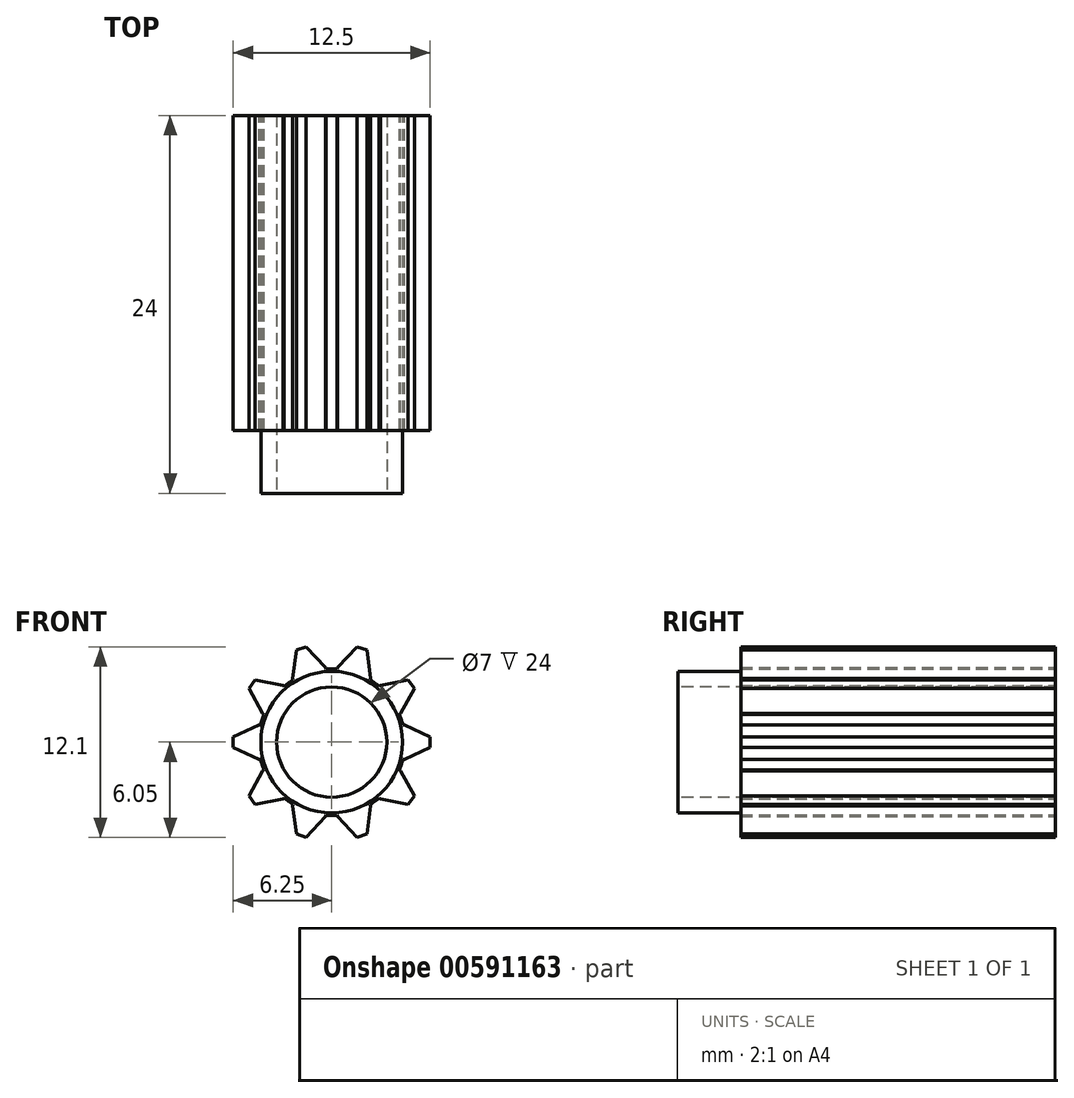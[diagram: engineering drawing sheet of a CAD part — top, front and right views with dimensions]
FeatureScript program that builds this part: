
annotation { "Feature Type Name" : "Feature", "Feature Type Description" : "" }
export const myFeature = defineFeature(function(context is Context, id is Id, definition is map)
    precondition{}
    {
        {
            var Q0;
            Q0=qCreatedBy(makeId("Front.planeOp"),FACE);
            var sketch = newSketch(context, id + "F0", { "sketchPlane" : qUnion([Q0])});
            skCircle(sketch, "E0", {"center": v(0, 0) * mm, "radius": 4.65 * mm});
            skLineSegment(sketch, "E1", {"start": v(0, 0) * mm, "end": v(4.65, 0) * mm, "construction": true});
            skLineSegment(sketch, "E2", {"start": v(4.65, 0) * mm, "end": v(6.25, 0) * mm, "construction": true});
            skLineSegment(sketch, "E3", {"start": v(6.25, 0) * mm, "end": v(6.25, 0.33) * mm});
            skLineSegment(sketch, "E4", {"start": v(4.52, 1.1) * mm, "end": v(4.62, 1.1) * mm});
            skLineSegment(sketch, "E5", {"start": v(4.62, 1.1) * mm, "end": v(6.25, 0.33) * mm});
            skLineSegment(sketch, "E6.MirrorCS", {"start": v(4.62, -1.1) * mm, "end": v(6.25, -0.33) * mm});
            skLineSegment(sketch, "E7.MirrorCS", {"start": v(6.25, 0) * mm, "end": v(6.25, -0.33) * mm});
            skLineSegment(sketch, "E8.MirrorCS", {"start": v(4.52, -1.1) * mm, "end": v(4.62, -1.1) * mm});
            skLineSegment(sketch, "E9.1.0", {"start": v(3, 3.55) * mm, "end": v(3.09, 3.6) * mm});
            skLineSegment(sketch, "E9.1.1", {"start": v(4.3, 1.77) * mm, "end": v(4.38, 1.82) * mm});
            skLineSegment(sketch, "E9.1.2", {"start": v(4.38, 1.82) * mm, "end": v(5.25, 3.4) * mm});
            skLineSegment(sketch, "E9.1.3", {"start": v(3.09, 3.6) * mm, "end": v(4.86, 3.94) * mm});
            skLineSegment(sketch, "E9.1.4", {"start": v(5.06, 3.67) * mm, "end": v(4.86, 3.94) * mm});
            skLineSegment(sketch, "E9.1.5", {"start": v(5.06, 3.67) * mm, "end": v(5.25, 3.4) * mm});
            skLineSegment(sketch, "E9.2.0", {"start": v(0.35, 4.64) * mm, "end": v(0.38, 4.73) * mm});
            skLineSegment(sketch, "E9.2.1", {"start": v(2.44, 3.96) * mm, "end": v(2.47, 4.05) * mm});
            skLineSegment(sketch, "E9.2.2", {"start": v(2.47, 4.05) * mm, "end": v(2.25, 5.84) * mm});
            skLineSegment(sketch, "E9.2.3", {"start": v(0.38, 4.73) * mm, "end": v(1.62, 6.05) * mm});
            skLineSegment(sketch, "E9.2.4", {"start": v(1.93, 5.94) * mm, "end": v(1.62, 6.05) * mm});
            skLineSegment(sketch, "E9.2.5", {"start": v(1.93, 5.94) * mm, "end": v(2.25, 5.84) * mm});
            skLineSegment(sketch, "E9.3.0", {"start": v(-2.44, 3.96) * mm, "end": v(-2.47, 4.05) * mm});
            skLineSegment(sketch, "E9.3.1", {"start": v(-0.35, 4.64) * mm, "end": v(-0.38, 4.73) * mm});
            skLineSegment(sketch, "E9.3.2", {"start": v(-0.38, 4.73) * mm, "end": v(-1.62, 6.05) * mm});
            skLineSegment(sketch, "E9.3.3", {"start": v(-2.47, 4.05) * mm, "end": v(-2.25, 5.84) * mm});
            skLineSegment(sketch, "E9.3.4", {"start": v(-1.93, 5.94) * mm, "end": v(-2.25, 5.84) * mm});
            skLineSegment(sketch, "E9.3.5", {"start": v(-1.93, 5.94) * mm, "end": v(-1.62, 6.05) * mm});
            skLineSegment(sketch, "E9.4.0", {"start": v(-4.3, 1.77) * mm, "end": v(-4.38, 1.82) * mm});
            skLineSegment(sketch, "E9.4.1", {"start": v(-3, 3.55) * mm, "end": v(-3.09, 3.6) * mm});
            skLineSegment(sketch, "E9.4.2", {"start": v(-3.09, 3.6) * mm, "end": v(-4.86, 3.94) * mm});
            skLineSegment(sketch, "E9.4.3", {"start": v(-4.38, 1.82) * mm, "end": v(-5.25, 3.4) * mm});
            skLineSegment(sketch, "E9.4.4", {"start": v(-5.06, 3.67) * mm, "end": v(-5.25, 3.4) * mm});
            skLineSegment(sketch, "E9.4.5", {"start": v(-5.06, 3.67) * mm, "end": v(-4.86, 3.94) * mm});
            skLineSegment(sketch, "E9.5.0", {"start": v(-4.52, -1.1) * mm, "end": v(-4.62, -1.1) * mm});
            skLineSegment(sketch, "E9.5.1", {"start": v(-4.52, 1.1) * mm, "end": v(-4.62, 1.1) * mm});
            skLineSegment(sketch, "E9.5.2", {"start": v(-4.62, 1.1) * mm, "end": v(-6.25, 0.33) * mm});
            skLineSegment(sketch, "E9.5.3", {"start": v(-4.62, -1.1) * mm, "end": v(-6.25, -0.33) * mm});
            skLineSegment(sketch, "E9.5.4", {"start": v(-6.25, 0) * mm, "end": v(-6.25, -0.33) * mm});
            skLineSegment(sketch, "E9.5.5", {"start": v(-6.25, 0) * mm, "end": v(-6.25, 0.33) * mm});
            skLineSegment(sketch, "E9.6.0", {"start": v(-3, -3.55) * mm, "end": v(-3.09, -3.6) * mm});
            skLineSegment(sketch, "E9.6.1", {"start": v(-4.3, -1.77) * mm, "end": v(-4.38, -1.82) * mm});
            skLineSegment(sketch, "E9.6.2", {"start": v(-4.38, -1.82) * mm, "end": v(-5.25, -3.4) * mm});
            skLineSegment(sketch, "E9.6.3", {"start": v(-3.09, -3.6) * mm, "end": v(-4.86, -3.94) * mm});
            skLineSegment(sketch, "E9.6.4", {"start": v(-5.06, -3.67) * mm, "end": v(-4.86, -3.94) * mm});
            skLineSegment(sketch, "E9.6.5", {"start": v(-5.06, -3.67) * mm, "end": v(-5.25, -3.4) * mm});
            skLineSegment(sketch, "E9.7.0", {"start": v(-0.35, -4.64) * mm, "end": v(-0.38, -4.73) * mm});
            skLineSegment(sketch, "E9.7.1", {"start": v(-2.44, -3.96) * mm, "end": v(-2.47, -4.05) * mm});
            skLineSegment(sketch, "E9.7.2", {"start": v(-2.47, -4.05) * mm, "end": v(-2.25, -5.84) * mm});
            skLineSegment(sketch, "E9.7.3", {"start": v(-0.38, -4.73) * mm, "end": v(-1.62, -6.05) * mm});
            skLineSegment(sketch, "E9.7.4", {"start": v(-1.93, -5.94) * mm, "end": v(-1.62, -6.05) * mm});
            skLineSegment(sketch, "E9.7.5", {"start": v(-1.93, -5.94) * mm, "end": v(-2.25, -5.84) * mm});
            skLineSegment(sketch, "E9.8.0", {"start": v(2.44, -3.96) * mm, "end": v(2.47, -4.05) * mm});
            skLineSegment(sketch, "E9.8.1", {"start": v(0.35, -4.64) * mm, "end": v(0.38, -4.73) * mm});
            skLineSegment(sketch, "E9.8.2", {"start": v(0.38, -4.73) * mm, "end": v(1.62, -6.05) * mm});
            skLineSegment(sketch, "E9.8.3", {"start": v(2.47, -4.05) * mm, "end": v(2.25, -5.84) * mm});
            skLineSegment(sketch, "E9.8.4", {"start": v(1.93, -5.94) * mm, "end": v(2.25, -5.84) * mm});
            skLineSegment(sketch, "E9.8.5", {"start": v(1.93, -5.94) * mm, "end": v(1.62, -6.05) * mm});
            skLineSegment(sketch, "E9.9.0", {"start": v(4.3, -1.77) * mm, "end": v(4.38, -1.82) * mm});
            skLineSegment(sketch, "E9.9.1", {"start": v(3, -3.55) * mm, "end": v(3.09, -3.6) * mm});
            skLineSegment(sketch, "E9.9.2", {"start": v(3.09, -3.6) * mm, "end": v(4.86, -3.94) * mm});
            skLineSegment(sketch, "E9.9.3", {"start": v(4.38, -1.82) * mm, "end": v(5.25, -3.4) * mm});
            skLineSegment(sketch, "E9.9.4", {"start": v(5.06, -3.67) * mm, "end": v(5.25, -3.4) * mm});
            skLineSegment(sketch, "E9.9.5", {"start": v(5.06, -3.67) * mm, "end": v(4.86, -3.94) * mm});
            skSolve(sketch);
        }
        {
            var Q0;
            Q0=qSketchRegion(id+"F0",true);
            extrude(context, id + "F1", {"entities" : qUnion([Q0]), "depth" : 10 * mm, "offsetDistance" : 25.4 * mm, "hasSecondDirection" : true, "secondDirectionOppositeDirection" : true, "secondDirectionDepth" : 10 * mm});
        }
        {
            var Q0;
            Q0=makeQuery(id+"F1.opExtrude","CAP_FACE",FACE,{"disambiguationData":[OSD([sQuery(id+"F0.wireOp",EDGE,"E0"),sQuery(id+"F0.wireOp",EDGE,"E3"),sQuery(id+"F0.wireOp",EDGE,"E4"),sQuery(id+"F0.wireOp",EDGE,"E5"),sQuery(id+"F0.wireOp",EDGE,"E6.MirrorCS"),sQuery(id+"F0.wireOp",EDGE,"E7.MirrorCS"),sQuery(id+"F0.wireOp",EDGE,"E8.MirrorCS"),sQuery(id+"F0.wireOp",EDGE,"9f6130ec-3d1a-4bbb-9d9a-4e7b52390a97.1.0"),sQuery(id+"F0.wireOp",EDGE,"9f6130ec-3d1a-4bbb-9d9a-4e7b52390a97.1.1"),sQuery(id+"F0.wireOp",EDGE,"9f6130ec-3d1a-4bbb-9d9a-4e7b52390a97.1.2"),sQuery(id+"F0.wireOp",EDGE,"9f6130ec-3d1a-4bbb-9d9a-4e7b52390a97.1.3"),sQuery(id+"F0.wireOp",EDGE,"9f6130ec-3d1a-4bbb-9d9a-4e7b52390a97.1.4"),sQuery(id+"F0.wireOp",EDGE,"9f6130ec-3d1a-4bbb-9d9a-4e7b52390a97.1.5"),sQuery(id+"F0.wireOp",EDGE,"9f6130ec-3d1a-4bbb-9d9a-4e7b52390a97.2.0"),sQuery(id+"F0.wireOp",EDGE,"9f6130ec-3d1a-4bbb-9d9a-4e7b52390a97.2.1"),sQuery(id+"F0.wireOp",EDGE,"9f6130ec-3d1a-4bbb-9d9a-4e7b52390a97.2.2"),sQuery(id+"F0.wireOp",EDGE,"9f6130ec-3d1a-4bbb-9d9a-4e7b52390a97.2.3"),sQuery(id+"F0.wireOp",EDGE,"9f6130ec-3d1a-4bbb-9d9a-4e7b52390a97.2.4"),sQuery(id+"F0.wireOp",EDGE,"9f6130ec-3d1a-4bbb-9d9a-4e7b52390a97.2.5"),sQuery(id+"F0.wireOp",EDGE,"9f6130ec-3d1a-4bbb-9d9a-4e7b52390a97.3.0"),sQuery(id+"F0.wireOp",EDGE,"9f6130ec-3d1a-4bbb-9d9a-4e7b52390a97.3.1"),sQuery(id+"F0.wireOp",EDGE,"9f6130ec-3d1a-4bbb-9d9a-4e7b52390a97.3.2"),sQuery(id+"F0.wireOp",EDGE,"9f6130ec-3d1a-4bbb-9d9a-4e7b52390a97.3.3"),sQuery(id+"F0.wireOp",EDGE,"9f6130ec-3d1a-4bbb-9d9a-4e7b52390a97.3.4"),sQuery(id+"F0.wireOp",EDGE,"9f6130ec-3d1a-4bbb-9d9a-4e7b52390a97.3.5"),sQuery(id+"F0.wireOp",EDGE,"9f6130ec-3d1a-4bbb-9d9a-4e7b52390a97.4.0"),sQuery(id+"F0.wireOp",EDGE,"9f6130ec-3d1a-4bbb-9d9a-4e7b52390a97.4.1"),sQuery(id+"F0.wireOp",EDGE,"9f6130ec-3d1a-4bbb-9d9a-4e7b52390a97.4.2"),sQuery(id+"F0.wireOp",EDGE,"9f6130ec-3d1a-4bbb-9d9a-4e7b52390a97.4.3"),sQuery(id+"F0.wireOp",EDGE,"9f6130ec-3d1a-4bbb-9d9a-4e7b52390a97.4.4"),sQuery(id+"F0.wireOp",EDGE,"9f6130ec-3d1a-4bbb-9d9a-4e7b52390a97.4.5"),sQuery(id+"F0.wireOp",EDGE,"9f6130ec-3d1a-4bbb-9d9a-4e7b52390a97.5.0"),sQuery(id+"F0.wireOp",EDGE,"9f6130ec-3d1a-4bbb-9d9a-4e7b52390a97.5.1"),sQuery(id+"F0.wireOp",EDGE,"9f6130ec-3d1a-4bbb-9d9a-4e7b52390a97.5.2"),sQuery(id+"F0.wireOp",EDGE,"9f6130ec-3d1a-4bbb-9d9a-4e7b52390a97.5.3"),sQuery(id+"F0.wireOp",EDGE,"9f6130ec-3d1a-4bbb-9d9a-4e7b52390a97.5.4"),sQuery(id+"F0.wireOp",EDGE,"9f6130ec-3d1a-4bbb-9d9a-4e7b52390a97.5.5"),sQuery(id+"F0.wireOp",EDGE,"9f6130ec-3d1a-4bbb-9d9a-4e7b52390a97.6.0"),sQuery(id+"F0.wireOp",EDGE,"9f6130ec-3d1a-4bbb-9d9a-4e7b52390a97.6.1"),sQuery(id+"F0.wireOp",EDGE,"9f6130ec-3d1a-4bbb-9d9a-4e7b52390a97.6.2"),sQuery(id+"F0.wireOp",EDGE,"9f6130ec-3d1a-4bbb-9d9a-4e7b52390a97.6.3"),sQuery(id+"F0.wireOp",EDGE,"9f6130ec-3d1a-4bbb-9d9a-4e7b52390a97.6.4"),sQuery(id+"F0.wireOp",EDGE,"9f6130ec-3d1a-4bbb-9d9a-4e7b52390a97.6.5"),sQuery(id+"F0.wireOp",EDGE,"9f6130ec-3d1a-4bbb-9d9a-4e7b52390a97.7.0"),sQuery(id+"F0.wireOp",EDGE,"9f6130ec-3d1a-4bbb-9d9a-4e7b52390a97.7.1"),sQuery(id+"F0.wireOp",EDGE,"9f6130ec-3d1a-4bbb-9d9a-4e7b52390a97.7.2"),sQuery(id+"F0.wireOp",EDGE,"9f6130ec-3d1a-4bbb-9d9a-4e7b52390a97.7.3"),sQuery(id+"F0.wireOp",EDGE,"9f6130ec-3d1a-4bbb-9d9a-4e7b52390a97.7.4"),sQuery(id+"F0.wireOp",EDGE,"9f6130ec-3d1a-4bbb-9d9a-4e7b52390a97.7.5"),sQuery(id+"F0.wireOp",EDGE,"9f6130ec-3d1a-4bbb-9d9a-4e7b52390a97.8.0"),sQuery(id+"F0.wireOp",EDGE,"9f6130ec-3d1a-4bbb-9d9a-4e7b52390a97.8.1"),sQuery(id+"F0.wireOp",EDGE,"9f6130ec-3d1a-4bbb-9d9a-4e7b52390a97.8.2"),sQuery(id+"F0.wireOp",EDGE,"9f6130ec-3d1a-4bbb-9d9a-4e7b52390a97.8.3"),sQuery(id+"F0.wireOp",EDGE,"9f6130ec-3d1a-4bbb-9d9a-4e7b52390a97.8.4"),sQuery(id+"F0.wireOp",EDGE,"9f6130ec-3d1a-4bbb-9d9a-4e7b52390a97.8.5"),sQuery(id+"F0.wireOp",EDGE,"9f6130ec-3d1a-4bbb-9d9a-4e7b52390a97.9.0"),sQuery(id+"F0.wireOp",EDGE,"9f6130ec-3d1a-4bbb-9d9a-4e7b52390a97.9.1"),sQuery(id+"F0.wireOp",EDGE,"9f6130ec-3d1a-4bbb-9d9a-4e7b52390a97.9.2"),sQuery(id+"F0.wireOp",EDGE,"9f6130ec-3d1a-4bbb-9d9a-4e7b52390a97.9.3"),sQuery(id+"F0.wireOp",EDGE,"9f6130ec-3d1a-4bbb-9d9a-4e7b52390a97.9.4"),sQuery(id+"F0.wireOp",EDGE,"9f6130ec-3d1a-4bbb-9d9a-4e7b52390a97.9.5"),sQuery(id+"F0.wireOp",EDGE,"9f6130ec-3d1a-4bbb-9d9a-4e7b52390a97.10.0"),sQuery(id+"F0.wireOp",EDGE,"9f6130ec-3d1a-4bbb-9d9a-4e7b52390a97.10.1"),sQuery(id+"F0.wireOp",EDGE,"9f6130ec-3d1a-4bbb-9d9a-4e7b52390a97.10.2"),sQuery(id+"F0.wireOp",EDGE,"9f6130ec-3d1a-4bbb-9d9a-4e7b52390a97.10.3"),sQuery(id+"F0.wireOp",EDGE,"9f6130ec-3d1a-4bbb-9d9a-4e7b52390a97.10.4"),sQuery(id+"F0.wireOp",EDGE,"9f6130ec-3d1a-4bbb-9d9a-4e7b52390a97.10.5"),sQuery(id+"F0.wireOp",EDGE,"9f6130ec-3d1a-4bbb-9d9a-4e7b52390a97.11.0"),sQuery(id+"F0.wireOp",EDGE,"9f6130ec-3d1a-4bbb-9d9a-4e7b52390a97.11.1"),sQuery(id+"F0.wireOp",EDGE,"9f6130ec-3d1a-4bbb-9d9a-4e7b52390a97.11.2"),sQuery(id+"F0.wireOp",EDGE,"9f6130ec-3d1a-4bbb-9d9a-4e7b52390a97.11.3"),sQuery(id+"F0.wireOp",EDGE,"9f6130ec-3d1a-4bbb-9d9a-4e7b52390a97.11.4"),sQuery(id+"F0.wireOp",EDGE,"9f6130ec-3d1a-4bbb-9d9a-4e7b52390a97.11.5"),sQuery(id+"F0.wireOp",EDGE,"9f6130ec-3d1a-4bbb-9d9a-4e7b52390a97.12.0"),sQuery(id+"F0.wireOp",EDGE,"9f6130ec-3d1a-4bbb-9d9a-4e7b52390a97.12.1"),sQuery(id+"F0.wireOp",EDGE,"9f6130ec-3d1a-4bbb-9d9a-4e7b52390a97.12.2"),sQuery(id+"F0.wireOp",EDGE,"9f6130ec-3d1a-4bbb-9d9a-4e7b52390a97.12.3"),sQuery(id+"F0.wireOp",EDGE,"9f6130ec-3d1a-4bbb-9d9a-4e7b52390a97.12.4"),sQuery(id+"F0.wireOp",EDGE,"9f6130ec-3d1a-4bbb-9d9a-4e7b52390a97.12.5"),sQuery(id+"F0.wireOp",EDGE,"9f6130ec-3d1a-4bbb-9d9a-4e7b52390a97.13.0"),sQuery(id+"F0.wireOp",EDGE,"9f6130ec-3d1a-4bbb-9d9a-4e7b52390a97.13.1"),sQuery(id+"F0.wireOp",EDGE,"9f6130ec-3d1a-4bbb-9d9a-4e7b52390a97.13.2"),sQuery(id+"F0.wireOp",EDGE,"9f6130ec-3d1a-4bbb-9d9a-4e7b52390a97.13.3"),sQuery(id+"F0.wireOp",EDGE,"9f6130ec-3d1a-4bbb-9d9a-4e7b52390a97.13.4"),sQuery(id+"F0.wireOp",EDGE,"9f6130ec-3d1a-4bbb-9d9a-4e7b52390a97.13.5"),sQuery(id+"F0.wireOp",EDGE,"9f6130ec-3d1a-4bbb-9d9a-4e7b52390a97.14.0"),sQuery(id+"F0.wireOp",EDGE,"9f6130ec-3d1a-4bbb-9d9a-4e7b52390a97.14.1"),sQuery(id+"F0.wireOp",EDGE,"9f6130ec-3d1a-4bbb-9d9a-4e7b52390a97.14.2"),sQuery(id+"F0.wireOp",EDGE,"9f6130ec-3d1a-4bbb-9d9a-4e7b52390a97.14.3"),sQuery(id+"F0.wireOp",EDGE,"9f6130ec-3d1a-4bbb-9d9a-4e7b52390a97.14.4"),sQuery(id+"F0.wireOp",EDGE,"9f6130ec-3d1a-4bbb-9d9a-4e7b52390a97.14.5"),sQuery(id+"F0.wireOp",EDGE,"9f6130ec-3d1a-4bbb-9d9a-4e7b52390a97.15.0"),sQuery(id+"F0.wireOp",EDGE,"9f6130ec-3d1a-4bbb-9d9a-4e7b52390a97.15.1"),sQuery(id+"F0.wireOp",EDGE,"9f6130ec-3d1a-4bbb-9d9a-4e7b52390a97.15.2"),sQuery(id+"F0.wireOp",EDGE,"9f6130ec-3d1a-4bbb-9d9a-4e7b52390a97.15.3"),sQuery(id+"F0.wireOp",EDGE,"9f6130ec-3d1a-4bbb-9d9a-4e7b52390a97.15.4"),sQuery(id+"F0.wireOp",EDGE,"9f6130ec-3d1a-4bbb-9d9a-4e7b52390a97.15.5"),sQuery(id+"F0.wireOp",EDGE,"9f6130ec-3d1a-4bbb-9d9a-4e7b52390a97.16.0"),sQuery(id+"F0.wireOp",EDGE,"9f6130ec-3d1a-4bbb-9d9a-4e7b52390a97.16.1"),sQuery(id+"F0.wireOp",EDGE,"9f6130ec-3d1a-4bbb-9d9a-4e7b52390a97.16.2"),sQuery(id+"F0.wireOp",EDGE,"9f6130ec-3d1a-4bbb-9d9a-4e7b52390a97.16.3"),sQuery(id+"F0.wireOp",EDGE,"9f6130ec-3d1a-4bbb-9d9a-4e7b52390a97.16.4"),sQuery(id+"F0.wireOp",EDGE,"9f6130ec-3d1a-4bbb-9d9a-4e7b52390a97.16.5"),sQuery(id+"F0.wireOp",EDGE,"9f6130ec-3d1a-4bbb-9d9a-4e7b52390a97.17.0"),sQuery(id+"F0.wireOp",EDGE,"9f6130ec-3d1a-4bbb-9d9a-4e7b52390a97.17.1"),sQuery(id+"F0.wireOp",EDGE,"9f6130ec-3d1a-4bbb-9d9a-4e7b52390a97.17.2"),sQuery(id+"F0.wireOp",EDGE,"9f6130ec-3d1a-4bbb-9d9a-4e7b52390a97.17.3"),sQuery(id+"F0.wireOp",EDGE,"9f6130ec-3d1a-4bbb-9d9a-4e7b52390a97.17.4"),sQuery(id+"F0.wireOp",EDGE,"9f6130ec-3d1a-4bbb-9d9a-4e7b52390a97.17.5"),sQuery(id+"F0.wireOp",EDGE,"9f6130ec-3d1a-4bbb-9d9a-4e7b52390a97.18.0"),sQuery(id+"F0.wireOp",EDGE,"9f6130ec-3d1a-4bbb-9d9a-4e7b52390a97.18.1"),sQuery(id+"F0.wireOp",EDGE,"9f6130ec-3d1a-4bbb-9d9a-4e7b52390a97.18.2"),sQuery(id+"F0.wireOp",EDGE,"9f6130ec-3d1a-4bbb-9d9a-4e7b52390a97.18.3"),sQuery(id+"F0.wireOp",EDGE,"9f6130ec-3d1a-4bbb-9d9a-4e7b52390a97.18.4"),sQuery(id+"F0.wireOp",EDGE,"9f6130ec-3d1a-4bbb-9d9a-4e7b52390a97.18.5"),sQuery(id+"F0.wireOp",EDGE,"9f6130ec-3d1a-4bbb-9d9a-4e7b52390a97.19.0"),sQuery(id+"F0.wireOp",EDGE,"9f6130ec-3d1a-4bbb-9d9a-4e7b52390a97.19.1"),sQuery(id+"F0.wireOp",EDGE,"9f6130ec-3d1a-4bbb-9d9a-4e7b52390a97.19.2"),sQuery(id+"F0.wireOp",EDGE,"9f6130ec-3d1a-4bbb-9d9a-4e7b52390a97.19.3"),sQuery(id+"F0.wireOp",EDGE,"9f6130ec-3d1a-4bbb-9d9a-4e7b52390a97.19.4"),sQuery(id+"F0.wireOp",EDGE,"9f6130ec-3d1a-4bbb-9d9a-4e7b52390a97.19.5"),sQuery(id+"F0.wireOp",EDGE,"9f6130ec-3d1a-4bbb-9d9a-4e7b52390a97.20.0"),sQuery(id+"F0.wireOp",EDGE,"9f6130ec-3d1a-4bbb-9d9a-4e7b52390a97.20.1"),sQuery(id+"F0.wireOp",EDGE,"9f6130ec-3d1a-4bbb-9d9a-4e7b52390a97.20.2"),sQuery(id+"F0.wireOp",EDGE,"9f6130ec-3d1a-4bbb-9d9a-4e7b52390a97.20.3"),sQuery(id+"F0.wireOp",EDGE,"9f6130ec-3d1a-4bbb-9d9a-4e7b52390a97.20.4"),sQuery(id+"F0.wireOp",EDGE,"9f6130ec-3d1a-4bbb-9d9a-4e7b52390a97.20.5")])],"isStart":false});
            var sketch = newSketch(context, id + "F2", { "sketchPlane" : qUnion([Q0])});
            skCircle(sketch, "E10", {"center": v(0, 0) * mm, "radius": 4.5 * mm});
            skSolve(sketch);
        }
        {
            var Q0;
            Q0=qSketchRegion(id+"F2",true);
            extrude(context, id + "F3", {"entities" : qUnion([Q0]), "operationType" : NewBodyOperationType.ADD, "depth" : 4 * mm, "offsetDistance" : 25.4 * mm});
        }
        {
            var Q0;
            Q0=makeQuery(id+"F3.opExtrude","CAP_FACE",FACE,{"disambiguationData":[OSD([sQuery(id+"F2.wireOp",EDGE,"E10")])],"isStart":false});
            var sketch = newSketch(context, id + "F4", { "sketchPlane" : qUnion([Q0])});
            skCircle(sketch, "E11", {"center": v(0, 0) * mm, "radius": 3.5 * mm});
            skSolve(sketch);
        }
        {
            var Q0;
            Q0=qSketchRegion(id+"F4",true);
            extrude(context, id + "F5", {"entities" : qUnion([Q0]), "operationType" : NewBodyOperationType.REMOVE, "oppositeDirection" : true, "depth" : 25.25 * mm, "offsetDistance" : 25.4 * mm});
        }
    });
